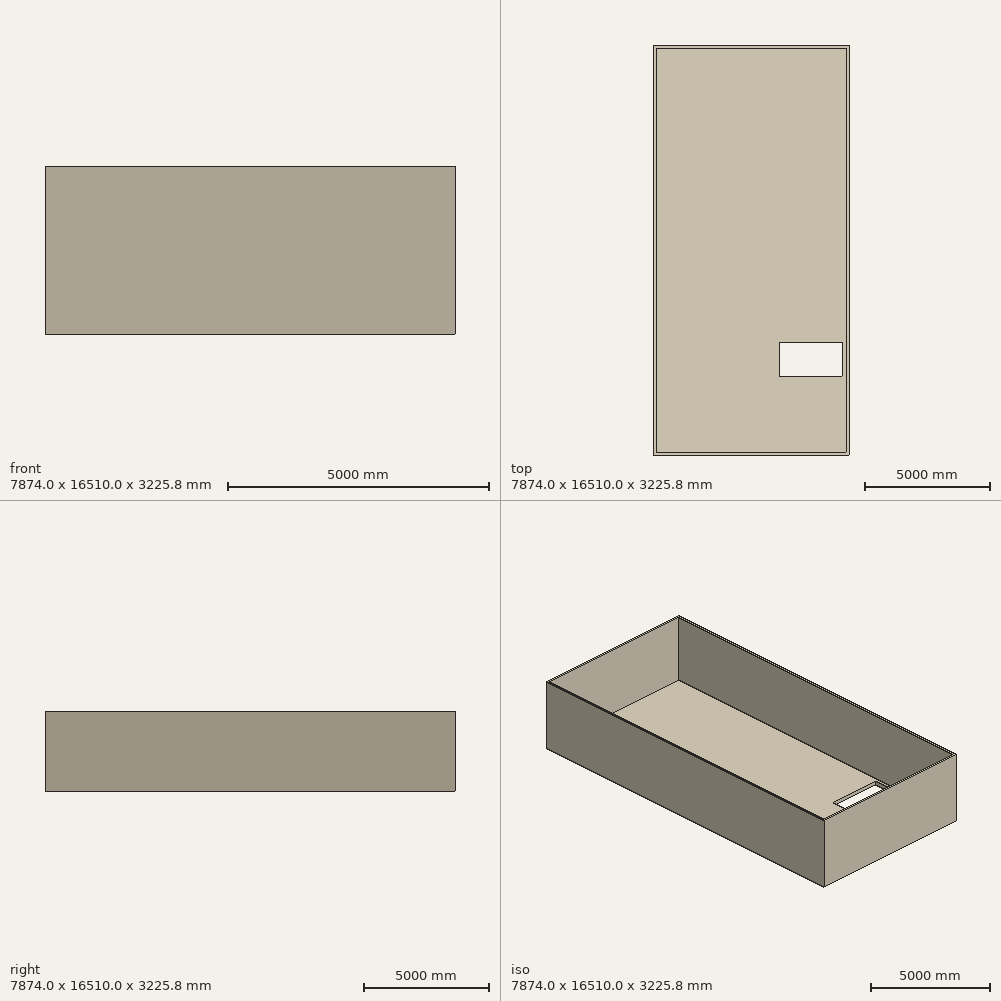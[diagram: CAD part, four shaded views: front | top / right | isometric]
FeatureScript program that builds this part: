
annotation { "Feature Type Name" : "Feature", "Feature Type Description" : "" }
export const myFeature = defineFeature(function(context is Context, id is Id, definition is map)
    precondition{}
    {
        {
            var Q0;
            Q0=qCreatedBy(makeId("Top.planeOp"),FACE);
            var sketch = newSketch(context, id + "F0", { "sketchPlane" : qUnion([Q0])});
            skLineSegment(sketch, "E0.bottom", {"start": v(-3937, -8255) * mm, "end": v(3937, -8255) * mm});
            skLineSegment(sketch, "E0.top", {"start": v(-3937, 8255) * mm, "end": v(3937, 8255) * mm});
            skLineSegment(sketch, "E0.left", {"start": v(-3937, -8255) * mm, "end": v(-3937, 8255) * mm});
            skLineSegment(sketch, "E0.right", {"start": v(3937, -8255) * mm, "end": v(3937, 8255) * mm});
            skLineSegment(sketch, "E1", {"start": v(0, 0) * mm, "end": v(0, -8255) * mm, "construction": true});
            skLineSegment(sketch, "E2", {"start": v(0, 0) * mm, "end": v(3937, 0) * mm, "construction": true});
            skPoint(sketch, "E2.endSnap0", {"position": v(3937, 0) * mm});
            skSolve(sketch);
        }
        {
            var Q0;
            Q0=qSketchRegion(id+"F0",true);
            extrude(context, id + "F1", {"entities" : qUnion([Q0]), "depth" : 177.8 * mm});
        }
        {
            var Q0;
            Q0=makeQuery(id+"F1.opExtrude","CAP_FACE",FACE,{"disambiguationData":[OSD([sQuery(id+"F0.wireOp",EDGE,"E0.bottom"),sQuery(id+"F0.wireOp",EDGE,"E0.top"),sQuery(id+"F0.wireOp",EDGE,"E0.left"),sQuery(id+"F0.wireOp",EDGE,"E0.right")])],"isStart":false});
            var sketch = newSketch(context, id + "F2", { "sketchPlane" : qUnion([Q0])});
            skLineSegment(sketch, "E3.0", {"start": v(-3835.4, 8153.4) * mm, "end": v(3835.4, 8153.4) * mm});
            skLineSegment(sketch, "E3.1", {"start": v(-3835.4, -8153.4) * mm, "end": v(-3835.4, 8153.4) * mm});
            skLineSegment(sketch, "E3.2", {"start": v(-3835.4, -8153.4) * mm, "end": v(3835.4, -8153.4) * mm});
            skLineSegment(sketch, "E3.3", {"start": v(3835.4, -8153.4) * mm, "end": v(3835.4, 8153.4) * mm});
            skLineSegment(sketch, "E4.1", {"start": v(-3937, 8255) * mm, "end": v(3937, 8255) * mm});
            skLineSegment(sketch, "E5.0", {"start": v(-3937, -8255) * mm, "end": v(-3937, 8255) * mm});
            skLineSegment(sketch, "E6.2", {"start": v(3937, -8255) * mm, "end": v(3937, 8255) * mm});
            skLineSegment(sketch, "E7.0", {"start": v(-3937, -8255) * mm, "end": v(3937, -8255) * mm});
            skSolve(sketch);
        }
        {
            var Q0;
            Q0=qSketchRegion(id+"F2",true);
            extrude(context, id + "F3", {"entities" : qUnion([Q0]), "operationType" : NewBodyOperationType.ADD, "depth" : 3048 * mm});
        }
        {
            var Q0;
            Q0=makeQuery(id+"F1.opExtrude","CAP_FACE",FACE,{"disambiguationData":[OSD([sQuery(id+"F0.wireOp",EDGE,"E0.bottom"),sQuery(id+"F0.wireOp",EDGE,"E0.top"),sQuery(id+"F0.wireOp",EDGE,"E0.left"),sQuery(id+"F0.wireOp",EDGE,"E0.right")])],"isStart":false});
            var sketch = newSketch(context, id + "F4", { "sketchPlane" : qUnion([Q0])});
            skLineSegment(sketch, "E8.bottom", {"start": v(3683, -3708.4) * mm, "end": v(1143, -3708.4) * mm});
            skLineSegment(sketch, "E8.top", {"start": v(3683, -5080) * mm, "end": v(1143, -5080) * mm});
            skLineSegment(sketch, "E8.left", {"start": v(3683, -3708.4) * mm, "end": v(3683, -5080) * mm});
            skLineSegment(sketch, "E8.right", {"start": v(1143, -3708.4) * mm, "end": v(1143, -5080) * mm});
            skSolve(sketch);
        }
        {
            var Q0;
            Q0=qSketchRegion(id+"F4",true);
            extrude(context, id + "F5", {"entities" : qUnion([Q0]), "operationType" : NewBodyOperationType.REMOVE, "endBound" : BoundingType.THROUGH_ALL, "oppositeDirection" : true, "depth" : 25.4 * mm});
        }
    });
